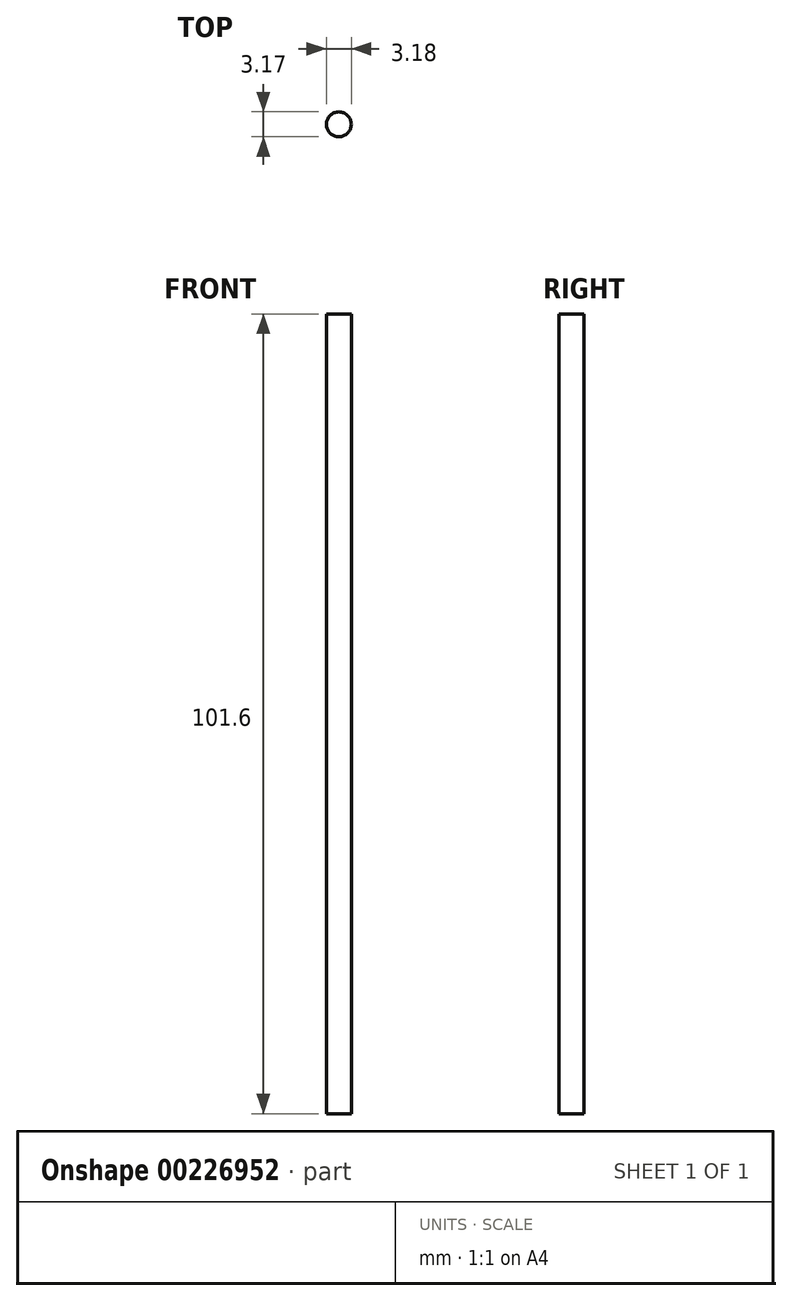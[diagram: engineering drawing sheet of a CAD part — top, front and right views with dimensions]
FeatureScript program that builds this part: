
annotation { "Feature Type Name" : "Feature", "Feature Type Description" : "" }
export const myFeature = defineFeature(function(context is Context, id is Id, definition is map)
    precondition{}
    {
        {
            var Q0;
            Q0=qCreatedBy(makeId("Top.planeOp"),FACE);
            var sketch = newSketch(context, id + "F0", { "sketchPlane" : qUnion([Q0])});
            skCircle(sketch, "E0", {"center": v(-19.5, 38.32) * mm, "radius": 1.59 * mm});
            skSolve(sketch);
        }
        {
            var Q0;
            Q0 = qSketchRegion(id + "F0", true);
            extrude(context, id + "F1", {"entities" : qUnion([Q0]), "depth" : 101.6 * mm});
        }
    });
